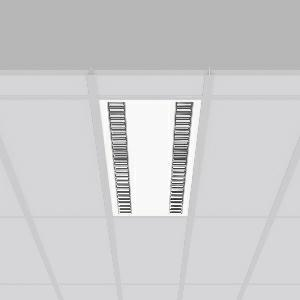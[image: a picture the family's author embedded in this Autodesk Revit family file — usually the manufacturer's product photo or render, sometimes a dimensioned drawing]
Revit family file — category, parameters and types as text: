
# Revit family: sonis_901680_002_1_76_fe08
name_source: partatom
category: Lighting Fixtures
units: mm (PartAtom-declared; Revit-internal decimal feet)

## family parameters
Cut with Voids When Loaded = No
Host = Face
Light Source = No
Part Type = Normal
Room Calculation Point = No
Round Connector Dimension = Use Diameter
Shared = No

## types (1)
- SONIS (1 x LED Modul 840, 6500 lm, 4000)
    Apparent Load = 50 VA
    CIE Flux Codes = 83 100 100 100 100
    Color Rendering = 80
    Color Temperature = 4000
    Default Elevation = 1800 mm
    Description = Series: SONIS
High-efficiency lay-in luminaire for ceiling systems with visible mounting rails. Housing: metal, powder-coated. Alea optical system: Reflector structure (ABS, Aluminium-coated, highly polished) with integrated diffuser made of non-yellowing plastic (PMMA) opal for glare-free light at the workstation. Narrow beam, brilliant luminous effect. Suitable for Recessed ceiling mounting. Driver integrated. Perfect for office areas (RUG < 19) and environments with computer screens in accordance with EN 12464-1. 
Colour: white
Length: 1197 mm
Width: 297 mm
Cut-out length: 1175 mm
Cut-out width: 275 mm
Recess height: 27 mm
Lamp: LED
Socket: without socket
Colour temperature: 4000K
Colour rendering index (CRI): 80
System power: 50 W
Rated luminous flux: 6500 lm
Luminous efficiency: 130 lm/W
Control gear: Converter, dimmable, DALI
Protection class: I
Type of protection: IP 20
    Height = 0 mm  [stored 0 ft]
    Lamp = 1 x LED Modul 840
    Lamp Light Flux = 6500 lm
    Lamp count = 1
    Length = 1197 mm
    Lifetime = 50000 h
    Luminous efficacy = 130 lm/W
    Manufacturer = RZB
    ModVariant = No
    Model = 901680.002.1.76
    Mounting Place = Ceiling
    Mounting Type = Recessed
    Number of Poles = 1
    OnlyDefault = Yes
    Power Factor = 1
    Product Name = SONIS
    Product group = Recessed modular luminaires
    ProductGroupID = 406
    Protection Class = Protection class I
    Protection Degree = IP 20
    RLX_Detail_Level = 1
    RLX_Emergency_Light_Flux = 0 lm
    RLX_Emergency_Type = 0
    RLX_Emergency_Type_DB = No
    RlxData = <blob elided: 37605 chars, md5=fd6bf3c6>
    Socket = socket
    Standby Power = 0 W
    System Light Flux = 6500 lm
    System Power = 50 W
    Type Comments = Product without accessories
    Type Image = 901648.002.jpg
    URL = http://relux.com
    VarID = ---
    Voltage = 230 V
    Voltage Range = 220-240 V
    Weight = 0.00 kg
    Width = 297 mm

note: [stored X ft] marks values corroborated as IEEE doubles in the binary element streams (Revit-internal decimal feet)

## geometry (parser evidence)
native form markers: Blend x4, Sweep x11
no freeform markers — native parametric forms only
